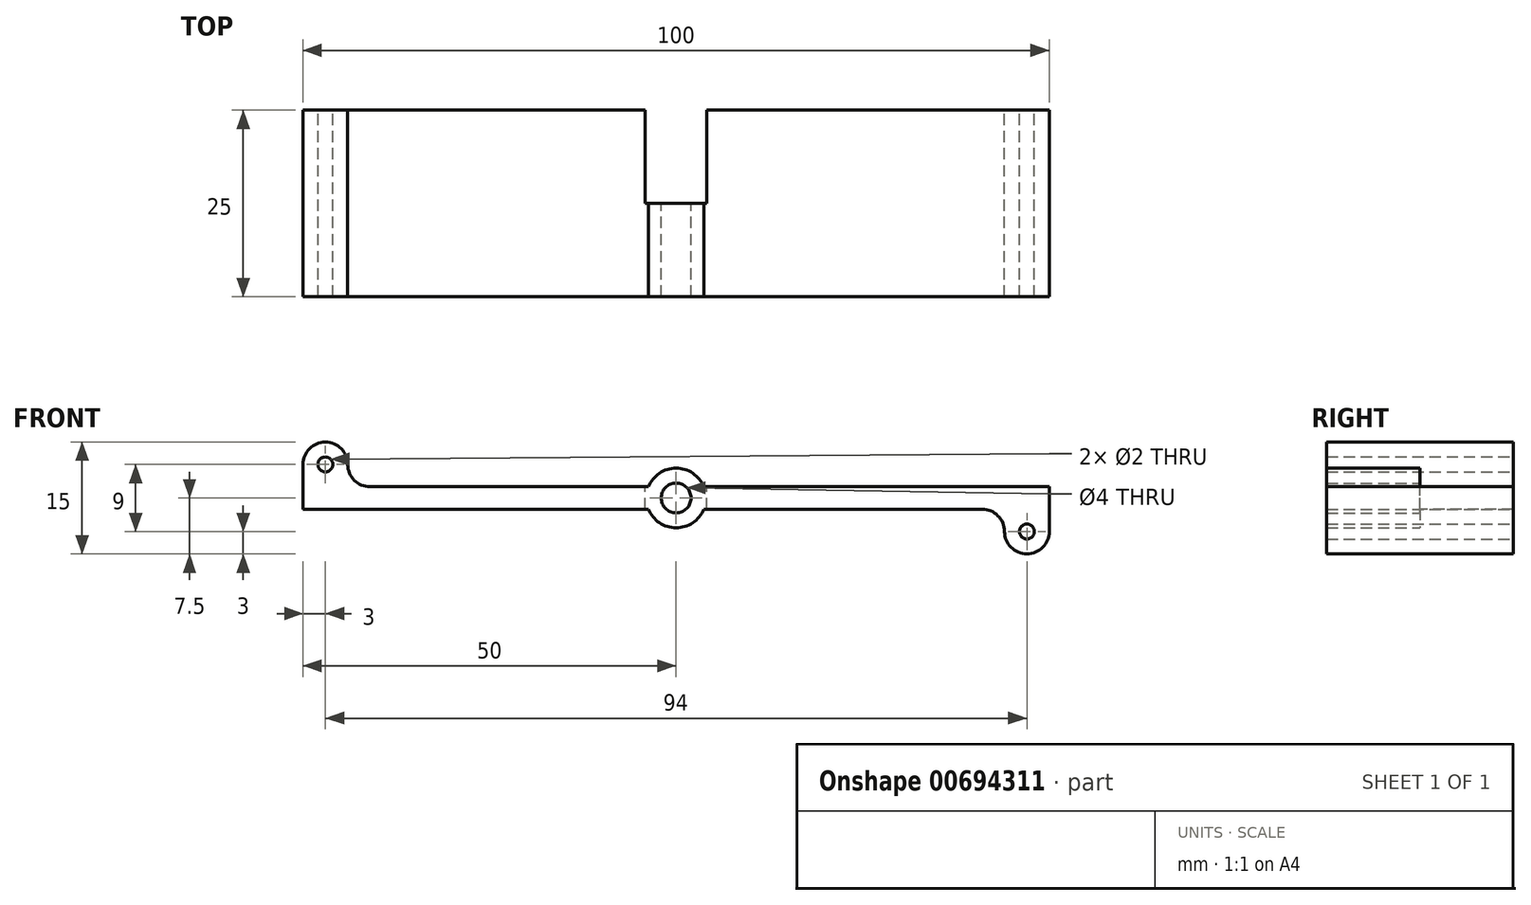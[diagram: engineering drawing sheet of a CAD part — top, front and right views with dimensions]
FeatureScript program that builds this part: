
annotation { "Feature Type Name" : "Feature", "Feature Type Description" : "" }
export const myFeature = defineFeature(function(context is Context, id is Id, definition is map)
    precondition{}
    {
        {
            var Q0;
            Q0=qCreatedBy(makeId("Front.planeOp"),FACE);
            var sketch = newSketch(context, id + "F0", { "sketchPlane" : qUnion([Q0])});
            skLineSegment(sketch, "E0.bottom", {"start": v(-41, 1.5) * mm, "end": v(-3.7, 1.5) * mm});
            skLineSegment(sketch, "E0.top", {"start": v(-50, -1.5) * mm, "end": v(-3.7, -1.5) * mm});
            skLineSegment(sketch, "E0.left", {"start": v(-50, 2.5) * mm, "end": v(-50, -1.5) * mm});
            skLineSegment(sketch, "E0.right", {"start": v(50, 1.5) * mm, "end": v(50, -1.5) * mm});
            skArc(sketch, "E1", {"start": v(-3.7, -1.5) * mm, "mid": v(0, -4) * mm, "end": v(3.7, -1.5) * mm});
            skLineSegment(sketch, "E2.trimOffspring", {"start": v(3.7, -1.5) * mm, "end": v(41, -1.5) * mm});
            skLineSegment(sketch, "E3.trimOffspring", {"start": v(3.7, 1.5) * mm, "end": v(50, 1.5) * mm});
            skArc(sketch, "E4.trimOffspring", {"start": v(3.7, 1.5) * mm, "mid": v(0, 4) * mm, "end": v(-3.7, 1.5) * mm});
            skCircle(sketch, "E5", {"center": v(0, 0) * mm, "radius": 2 * mm});
            skArc(sketch, "E6", {"start": v(-44, 4.5) * mm, "mid": v(-47, 7.5) * mm, "end": v(-50, 4.5) * mm});
            skCircle(sketch, "E7", {"center": v(-47, 4.5) * mm, "radius": 1 * mm});
            skLineSegment(sketch, "E8", {"start": v(-44, 4.5) * mm, "end": v(-44, 4.5) * mm});
            skLineSegment(sketch, "E9", {"start": v(-50, 4.5) * mm, "end": v(-50, 1.5) * mm});
            skArc(sketch, "E10.filletArc", {"start": v(-44, 4.5) * mm, "mid": v(-43.12, 2.38) * mm, "end": v(-41, 1.5) * mm});
            skArc(sketch, "E11", {"start": v(44, -4.5) * mm, "mid": v(47, -7.5) * mm, "end": v(50, -4.5) * mm});
            skLineSegment(sketch, "E12", {"start": v(50, -4.5) * mm, "end": v(50, -1.5) * mm});
            skCircle(sketch, "E13", {"center": v(47, -4.5) * mm, "radius": 1 * mm});
            skLineSegment(sketch, "E14", {"start": v(44, -4.5) * mm, "end": v(44, -4.5) * mm});
            skPoint(sketch, "E15.visualSharp", {"position": v(44, -1.5) * mm});
            skArc(sketch, "E15.filletArc", {"start": v(44, -4.5) * mm, "mid": v(43.12, -2.38) * mm, "end": v(41, -1.5) * mm});
            skSolve(sketch);
        }
        {
            var Q0;
            Q0 = qSketchRegion(id + "F0", true);
            extrude(context, id + "F1", {"entities" : qUnion([Q0]), "depth" : 25 * mm, "offsetDistance" : 25 * mm});
        }
        {
            var Q0;
            Q0=qCreatedBy(makeId("Top.planeOp"),FACE);
            var sketch = newSketch(context, id + "F2", { "sketchPlane" : qUnion([Q0])});
            skLineSegment(sketch, "E16.bottom", {"start": v(-4.12, 0) * mm, "end": v(4.12, 0) * mm});
            skLineSegment(sketch, "E16.top", {"start": v(-4.13, -12.5) * mm, "end": v(4.13, -12.5) * mm});
            skLineSegment(sketch, "E16.left", {"start": v(-4.12, 0) * mm, "end": v(-4.13, -12.5) * mm});
            skLineSegment(sketch, "E16.right", {"start": v(4.13, 0) * mm, "end": v(4.12, -12.5) * mm});
            skSolve(sketch);
        }
        {
            var Q0;
            Q0 = qSketchRegion(id + "F2", true);
            extrude(context, id + "F3", {"entities" : qUnion([Q0]), "operationType" : NewBodyOperationType.REMOVE, "endBound" : BoundingType.SYMMETRIC, "oppositeDirection" : true, "depth" : 25 * mm, "offsetDistance" : 25 * mm});
        }
    });
